# Revit family: Plumbing-Fixtures_Grohe_Flushing-Cistern_38863000_14_METRIC
name_source: partatom
category: Plumbing Fixtures
revit_build: Autodesk Revit 2014 (Build: 20130308_1515(x64)
units: mm (PartAtom-declared; Revit-internal decimal feet)

## types (1)
- Plumbing-Fixtures_Grohe_Flushing-Cistern_38863000_14_METRIC
    ADA Compliant = No
    Assembly Code = C1030220
    AssetType = Fixed
    CW Connection = Yes
    CWFU = 4.5
    ClassificationName = Uniclass 2015
    ClassificationValue = Pr_40_20_93_79
    Cold Water Connection Diameter = 10 mm  [stored 0.0328084 ft]
    Cost = 0 $
    Default Elevation = 600 mm
    Description = Uniset for WC
6 - 9 l adjustable
with small maintenance access
pneumatic discharge valve offering 3 modes of operation: dual flush or start/stop or single flush
PE outlet bend Ø 80 mm
inlet and outlet connecting set
steel frame, hot galvanized, with 4 fixing brackets
2 WC fixing bolts
distance of fixing bolts 180/230 mm
fixing device for ceramic
water supply connection from top
low noise (group I acc. to German Noise Specification)
test approval applied for
with plaster base coating made of vinyl fleece
angle valve ½
with push fit flexible hose union
shortable inspection shaft incl.
protection during construction phase,
for vertical use
without wall plate/actuation
GROHE EcoJoy® technology for less water and perfect flow
    DocumentationTechnical = http://cdn08.grohe.com
    DurationUnit = Years
    Ecojoy = No
    ExpectedLife = 0
    Faucet Material = ABS Plastic - White
    Features = Uniset for WC
6 - 9 l adjustable
with small maintenance access
pneumatic discharge valve offering 3 modes of operation: dual flush or start/stop or single flush
PE outlet bend Ø 80 mm
inlet and outlet connecting set
steel frame, hot galvanized, with 4 fixing brackets
2 WC fixing bolts
distance of fixing bolts 180/230 mm
fixing device for ceramic
water supply connection from top
low noise (group I acc. to German Noise Specification)
test approval applied for
with plaster base coating made of vinyl fleece
angle valve ½
with push fit flexible hose union
shortable inspection shaft incl.
protection during construction phase,
for vertical use
without wall plate/actuation
GROHE EcoJoy® technology for less water and perfect flow
    Frame Material = Steel, Paint Finish, Blue
    HW Connection = Yes
    HWFU = 4.5
    Height = 855 mm  [stored 2.80512 ft]
    Hot Water Connection Diameter = 10 mm  [stored 0.0328084 ft]
    Keynote = N13
    Length = 80 mm  [stored 0.262467 ft]
    Low Emitting Material = No
    Manufacturer = Grohe Limited
    Masterformat Number = 01 52 19
    Masterformat Title = Sanitary Facilities
    Model = Uniset For WC
    ModelNumber = 38863000
    NBSDescription = Urinal flushing valves;
    NBSObjectName = Urinal flushing valves;
    NBSReference = 45-35-70/355
    Product Documentation Link = http://cdn08.grohe.com
    Product Page URL = http://cdn08.grohe.com
    ProductionYear = 2016
    Size = 80mmx550mmx855mm
    Type Comments = 38863000
    TypeName = Uniset For WC
    URL = www.grohe.com
    Vent Connection = No
    WFU = 0
    WarrantyDurationUnit = Years
    Waste Connection = No
    Width = 550 mm
    _BIMspec_GUID = 0
    _current revision = 1
    _distributed by = www.bimstore.co.uk

note: [stored X ft] marks values corroborated as IEEE doubles in the binary element streams (Revit-internal decimal feet)

## geometry (parser evidence)
native form markers: Blend x6, Sweep x1
no freeform markers — native parametric forms only
